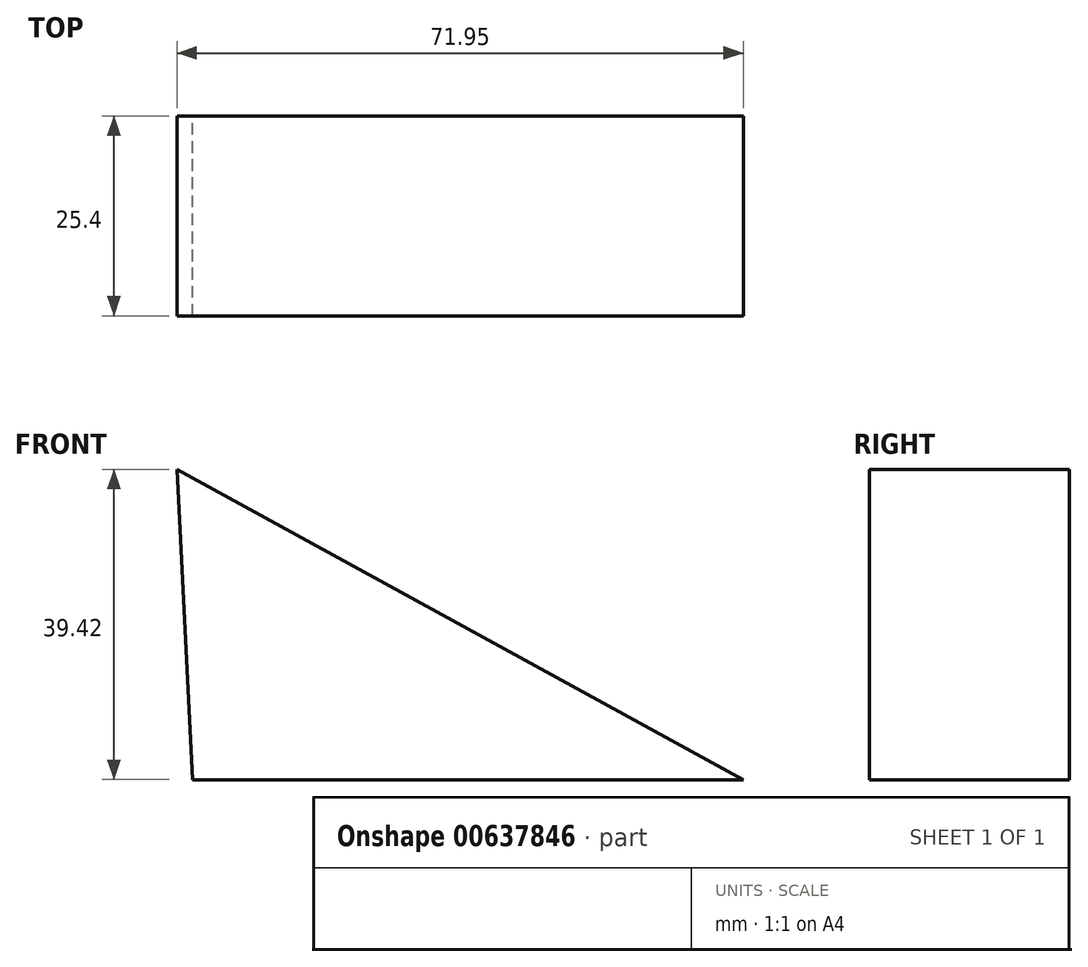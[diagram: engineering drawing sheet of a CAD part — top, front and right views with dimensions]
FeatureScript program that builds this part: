
annotation { "Feature Type Name" : "Feature", "Feature Type Description" : "" }
export const myFeature = defineFeature(function(context is Context, id is Id, definition is map)
    precondition{}
    {
        {
            var Q0;
            Q0=qCreatedBy(makeId("Front.planeOp"),FACE);
            var sketch = newSketch(context, id + "F0", { "sketchPlane" : qUnion([Q0])});
            skLineSegment(sketch, "E0", {"start": v(-40.72, 52.52) * mm, "end": v(31.23, 13.1) * mm});
            skLineSegment(sketch, "E1", {"start": v(-40.72, 52.52) * mm, "end": v(-38.7, 13.1) * mm});
            skLineSegment(sketch, "E2", {"start": v(-38.7, 13.1) * mm, "end": v(31.23, 13.1) * mm});
            skSolve(sketch);
        }
        {
            var Q0;
            Q0 = qSketchRegion(id + "F0", true);
            extrude(context, id + "F1", {"entities" : qUnion([Q0]), "depth" : 25.4 * mm, "offsetDistance" : 25.4 * mm});
        }
    });
